MODEL slx_3d19b643b928
KIND model
CONFIG AbsTol = auto
CONFIG FixedStep = auto
CONFIG MaxStep = auto
CONFIG MinStep = auto
CONFIG RelTol = 1e-3
CONFIG SampleTimeConstraint = Unconstrained
CONFIG Solver = FixedStepDiscrete
CONFIG SolverMode = SingleTasking
CONFIG SolverName = FixedStepDiscrete
CONFIG StartTime = 0.0
CONFIG StopTime = 100
BLOCK [Constant] Constant
  Value = 7
BLOCK [Delay] Delay
  DelayLength = 12
  InitialCondition = 0
  InputPortMap = u0
  Ports = [1, 1]
BLOCK [Delay] Delay1
  DelayLength = 6
  InitialCondition = 0
  InputPortMap = u0
  Ports = [1, 1]
BLOCK [Reference] HDL Counter  REF=hdlsllib/HDL Operations/HDL Counter
  Ports = [1, 1]
  SourceBlock = hdlsllib/HDL Operations/HDL Counter
  SourceType = HDL Counter
BLOCK [DiscretePulseGenerator] Pulse Generator
  Period = 3
  Ports = [0, 1]
BLOCK [DiscretePulseGenerator] Pulse Generator1
  Period = 50
  PhaseDelay = 2
  Ports = [0, 1]
BLOCK [Scope] Scope
  NumInputPorts = 8
  Ports = [8]
  ScopeSpecificationString = Simulink.scopes.TimeScopeBlockCfg('CurrentConfiguration', extmgr.ConfigurationSet(extmgr.Configuration('Core','General UI',true),extmgr.Configuration('Core','Source UI',true),extmgr.Configuration('Sources','WiredSimulink',true),extmgr.Configuration('Visuals','Time Domain',true,'SerializedDisplays',{struct('MinYLimReal','-0.125','MaxYLimReal','1.125','YLabelReal','','MinYLimMag','0.00000','MaxYLimM...<+6198ch>
BLOCK [DataTypeConversion] convert1
  OutDataTypeStr = fixdt(0,8,0)
  RndMeth = Floor
  SaturateOnIntegerOverflow = off
BLOCK [DataTypeConversion] convert2
  RndMeth = Floor
  SaturateOnIntegerOverflow = off
BLOCK [DataTypeConversion] convert3
  RndMeth = Floor
  SaturateOnIntegerOverflow = off
BLOCK [Reference] upcount  REF=lib_dsphdlcontrol_v1/upcount  (lib defined in slx_169a934beb0a)
  Ports = [3, 2]
  SourceBlock = lib_dsphdlcontrol_v1/upcount
  SourceType = A simple down counter.
ANNOTATION (root): Testbench Module: downcount
ANNOTATION (root): Author: Mike Babst
LINE Constant:1 -> convert1:1
LINE Delay1:1 -> convert2:1
LINE Delay:1 -> convert3:1
LINE HDL Counter:1 -> Scope:7
LINE Pulse Generator1:1 -> Delay1:1
LINE Pulse Generator:1 -> Delay:1
LINE convert1:1 -> upcount:1
NET convert2:1 -> Scope:1, upcount:2
NET convert3:1 -> HDL Counter:1, Scope:2, Scope:5, upcount:3
NET upcount:1 -> Scope:3, Scope:6
LINE upcount:2 -> Scope:4
note: NET lines group one-source signal fan-out (src -> all destinations, sorted); 1:1 wires keep LINE
